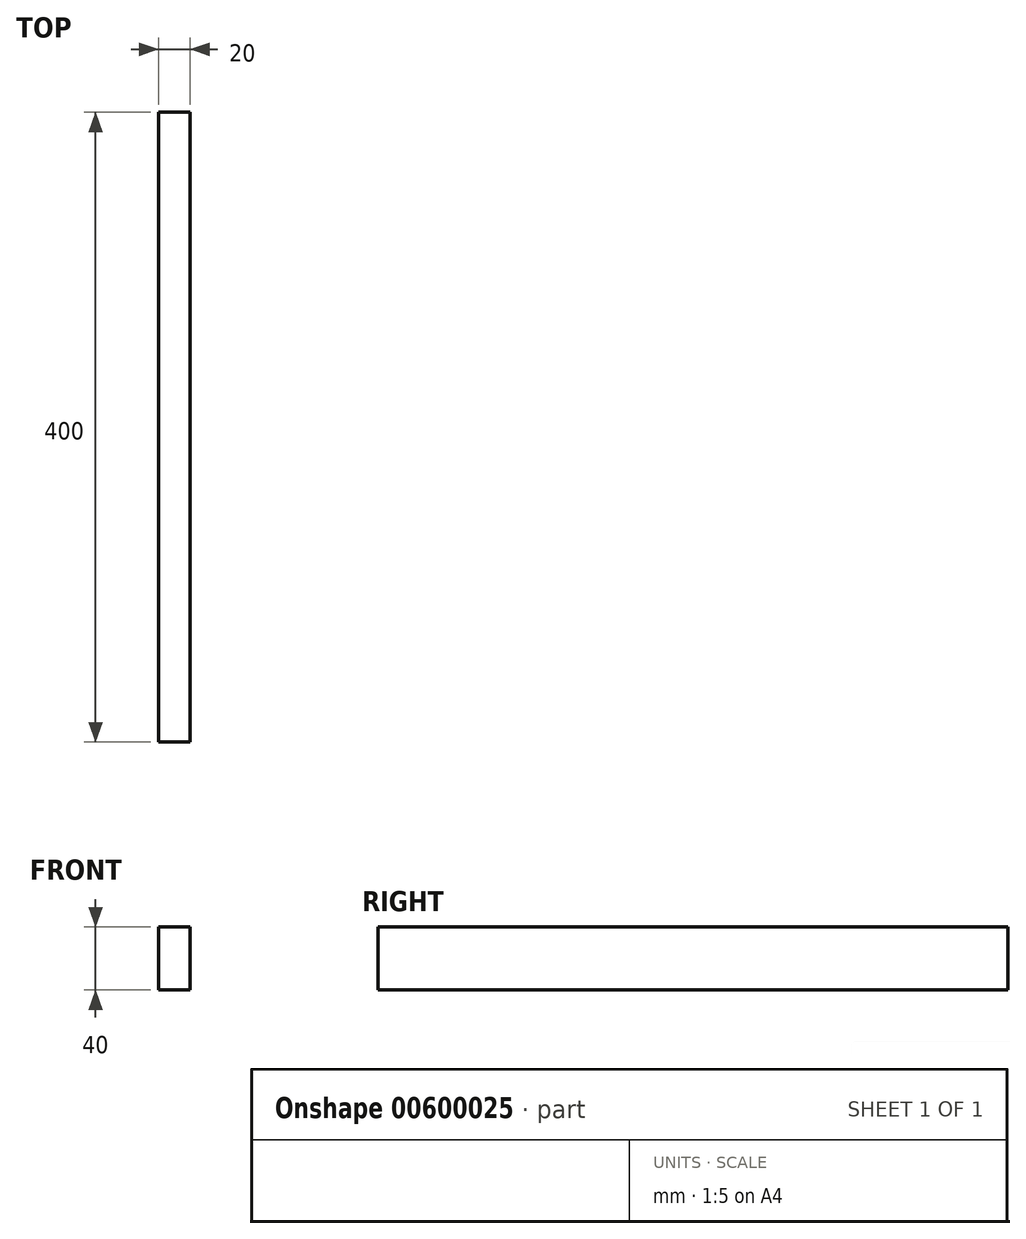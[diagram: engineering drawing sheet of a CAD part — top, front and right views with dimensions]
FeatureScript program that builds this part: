
annotation { "Feature Type Name" : "Feature", "Feature Type Description" : "" }
export const myFeature = defineFeature(function(context is Context, id is Id, definition is map)
    precondition{}
    {
        {
            var Q0;
            Q0=qCreatedBy(makeId("Front.planeOp"),FACE);
            var sketch = newSketch(context, id + "F0", { "sketchPlane" : qUnion([Q0])});
            skLineSegment(sketch, "E0.bottom", {"start": v(0, 0) * mm, "end": v(20, 0) * mm});
            skLineSegment(sketch, "E0.top", {"start": v(0, 40) * mm, "end": v(20, 40) * mm});
            skLineSegment(sketch, "E0.left", {"start": v(0, 0) * mm, "end": v(0, 40) * mm});
            skLineSegment(sketch, "E0.right", {"start": v(20, 0) * mm, "end": v(20, 40) * mm});
            skSolve(sketch);
        }
        {
            var Q0;
            Q0 = qSketchRegion(id + "F0", true);
            extrude(context, id + "F1", {"entities" : qUnion([Q0]), "depth" : 400 * mm, "offsetDistance" : 25 * mm, "symmetric" : true});
        }
    });
